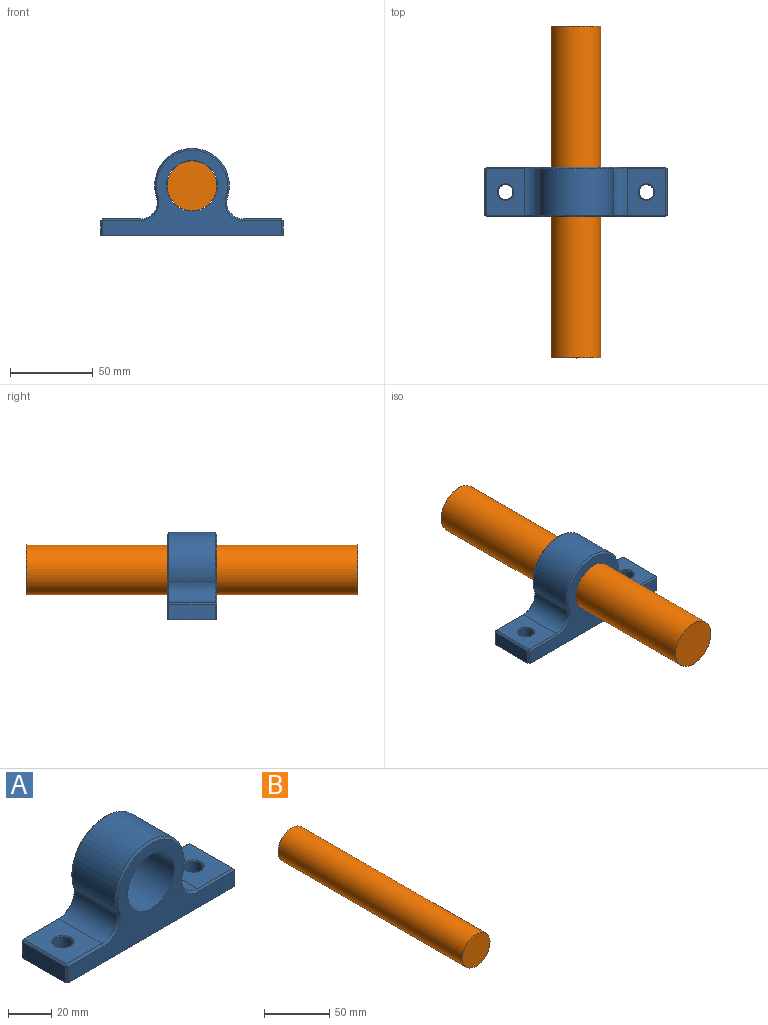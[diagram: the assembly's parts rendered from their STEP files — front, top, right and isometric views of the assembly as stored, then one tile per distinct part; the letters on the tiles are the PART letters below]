
ASSEMBLY  parts=2 mates=1
PART A: 37 faces, bbox 110x30x52.5 mm
  f0: plane 28x23.08mm, normal (0,0,1), area 567.6mm2, adj f10,f12,f15,f20,f36
  f1: plane 28x9mm, normal (-1,0,0), area 252mm2, adj f2,f11,f15,f16
  f2: plane 110x30mm, normal (0,0,-1), area 3140.9mm2, adj f1,f3,f7,f8,f11,f16,f21,f26
  f3: plane 28x9mm, normal (1,0,0), area 252mm2, adj f2,f21,f26,f27
  f4: plane 28x23.08mm, normal (0,0,1), area 567.6mm2, adj f9,f22,f27,f30,f34
  f5: cylinder r=15.25mm len=30.5mm, axis (0,1,0), area 2874.6mm2, adj f7,f8
  f6: cylinder r=22.5mm len=45mm, axis (0,1,0), area 2373.3mm2, adj f9,f10,f17,f25
  f7: plane 108x51.5mm, normal (0,-1,0), area 1873.7mm2, adj f2,f5,f11,f12,f14,f17,f19,f21
  f8: plane 108x51.5mm, normal (0,1,0), area 1873.7mm2, adj f2,f5,f16,f20,f23,f25,f26,f28
  f9: cylinder r=10mm len=28mm, axis (0,1,0), area 527.4mm2, adj f4,f6,f19,f28
  f10: cylinder r=10mm len=28mm, axis (0,1,0), area 527.4mm2, adj f0,f6,f14,f23
  f11: plane 9x1mm, normal (-0.71,-0.71,0), area 12.7mm2, adj f1,f2,f7,f13
  f12: plane 23.08x1mm, normal (0,-0.71,0.71), area 32.6mm2, adj f0,f7,f13,f14
  f13: plane 1x1mm, normal (-0.58,-0.58,0.58), area 0.9mm2, adj f11,f12,f15
  f14: cone r=11mm half-angle=45deg, axis (0,-1,0), area 28mm2, adj f7,f10,f12,f17
  f15: plane 28x1mm, normal (-0.71,0,0.71), area 39.6mm2, adj f0,f1,f13,f18
  f16: plane 9x1mm, normal (-0.71,0.71,0), area 12.7mm2, adj f1,f2,f8,f18
  f17: cone r=21.5mm half-angle=45deg, axis (0,1,0), area 117.2mm2, adj f6,f7,f14,f19
  f18: plane 1x1mm, normal (-0.58,0.58,0.58), area 0.9mm2, adj f15,f16,f20
  f19: cone r=11mm half-angle=45deg, axis (0,-1,0), area 28mm2, adj f7,f9,f17,f22
  f20: plane 23.08x1mm, normal (0,0.71,0.71), area 32.6mm2, adj f0,f8,f18,f23
  f21: plane 9x1mm, normal (0.71,-0.71,0), area 12.7mm2, adj f2,f3,f7,f24
  f22: plane 23.08x1mm, normal (0,-0.71,0.71), area 32.6mm2, adj f4,f7,f19,f24
  f23: cone r=11mm half-angle=45deg, axis (0,1,0), area 28mm2, adj f8,f10,f20,f25
  f24: plane 1x1mm, normal (0.58,-0.58,0.58), area 0.9mm2, adj f21,f22,f27
  f25: cone r=22.5mm half-angle=45deg, axis (0,-1,0), area 117.2mm2, adj f6,f8,f23,f28
  f26: plane 9x1mm, normal (0.71,0.71,0), area 12.7mm2, adj f2,f3,f8,f29
  f27: plane 28x1mm, normal (0.71,0,0.71), area 39.6mm2, adj f3,f4,f24,f29
  f28: cone r=11mm half-angle=45deg, axis (0,1,0), area 28mm2, adj f8,f9,f25,f30
  f29: plane 1x1mm, normal (0.58,0.58,0.58), area 0.9mm2, adj f26,f27,f30
  f30: plane 23.08x1mm, normal (0,0.71,0.71), area 32.6mm2, adj f4,f8,f28,f29
  f31: cylinder r=4.5mm len=9mm, axis (0,0,1), area 254.5mm2, adj f33,f34
  f32: cylinder r=4.5mm len=9mm, axis (0,0,1), area 254.5mm2, adj f35,f36
  f33: cone r=5mm half-angle=45deg, axis (0,0,-1), area 21.1mm2, adj f2,f31
  f34: cone r=4.5mm half-angle=45deg, axis (0,0,1), area 21.1mm2, adj f4,f31
  f35: cone r=5mm half-angle=45deg, axis (0,0,-1), area 21.1mm2, adj f2,f32
  f36: cone r=4.5mm half-angle=45deg, axis (0,0,1), area 21.1mm2, adj f0,f32
PART B: 3 faces, bbox 30x200x30 mm
  f0: cylinder r=15mm len=200mm, axis (0,1,0), area 18849.6mm2, adj f1,f2
  f1: plane 30x30mm, normal (0,-1,0), area 706.9mm2, adj f0
  f2: plane 30x30mm, normal (0,1,0), area 706.9mm2, adj f0
PLACE A t=(-58.12,13.02,26.12)mm
PLACE B t=(-58.12,-1.98,51.12)mm
MATE cylindrical B.f0 <-> A.f5  axis (0,1,0) through (-58.12,-1.98,51.12)mm
